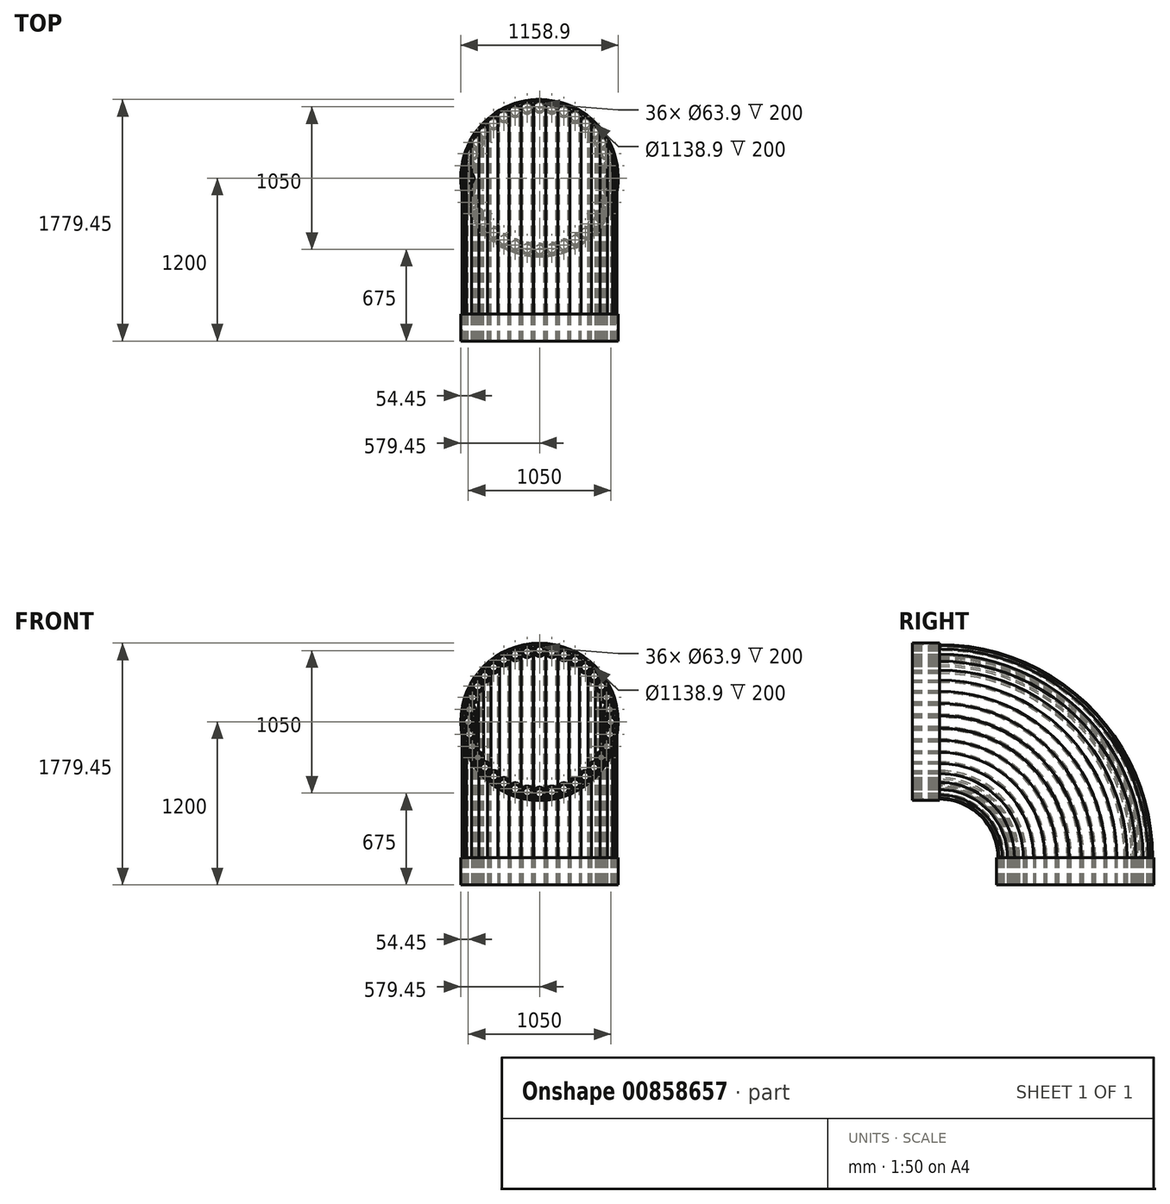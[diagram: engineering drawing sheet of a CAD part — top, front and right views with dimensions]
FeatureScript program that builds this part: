
annotation { "Feature Type Name" : "Feature", "Feature Type Description" : "" }
export const myFeature = defineFeature(function(context is Context, id is Id, definition is map)
    precondition{}
    {
        {
            var Q0;
            Q0=qCreatedBy(makeId("Front.planeOp"),FACE);
            var sketch = newSketch(context, id + "F0", { "sketchPlane" : qUnion([Q0])});
            skCircle(sketch, "E0", {"center": v(0, 0) * mm, "radius": 525 * mm, "construction": true});
            skCircle(sketch, "E1", {"center": v(0, 525) * mm, "radius": 44.45 * mm});
            skCircle(sketch, "E2", {"center": v(0, 525) * mm, "radius": 31.95 * mm});
            skCircle(sketch, "E3.1.0", {"center": v(-91.17, 517.02) * mm, "radius": 44.45 * mm});
            skCircle(sketch, "E3.1.1", {"center": v(-91.17, 517.02) * mm, "radius": 31.95 * mm});
            skCircle(sketch, "E3.2.0", {"center": v(-179.56, 493.34) * mm, "radius": 44.45 * mm});
            skCircle(sketch, "E3.2.1", {"center": v(-179.56, 493.34) * mm, "radius": 31.95 * mm});
            skCircle(sketch, "E3.3.0", {"center": v(-262.5, 454.66) * mm, "radius": 44.45 * mm});
            skCircle(sketch, "E3.3.1", {"center": v(-262.5, 454.66) * mm, "radius": 31.95 * mm});
            skCircle(sketch, "E3.4.0", {"center": v(-337.46, 402.17) * mm, "radius": 44.45 * mm});
            skCircle(sketch, "E3.4.1", {"center": v(-337.46, 402.17) * mm, "radius": 31.95 * mm});
            skCircle(sketch, "E3.5.0", {"center": v(-402.17, 337.46) * mm, "radius": 44.45 * mm});
            skCircle(sketch, "E3.5.1", {"center": v(-402.17, 337.46) * mm, "radius": 31.95 * mm});
            skCircle(sketch, "E3.6.0", {"center": v(-454.66, 262.5) * mm, "radius": 44.45 * mm});
            skCircle(sketch, "E3.6.1", {"center": v(-454.66, 262.5) * mm, "radius": 31.95 * mm});
            skCircle(sketch, "E3.7.0", {"center": v(-493.34, 179.56) * mm, "radius": 44.45 * mm});
            skCircle(sketch, "E3.7.1", {"center": v(-493.34, 179.56) * mm, "radius": 31.95 * mm});
            skCircle(sketch, "E3.8.0", {"center": v(-517.02, 91.17) * mm, "radius": 44.45 * mm});
            skCircle(sketch, "E3.8.1", {"center": v(-517.02, 91.17) * mm, "radius": 31.95 * mm});
            skCircle(sketch, "E3.9.0", {"center": v(-525, 0) * mm, "radius": 44.45 * mm});
            skCircle(sketch, "E3.9.1", {"center": v(-525, 0) * mm, "radius": 31.95 * mm});
            skCircle(sketch, "E3.10.0", {"center": v(-517.02, -91.17) * mm, "radius": 44.45 * mm});
            skCircle(sketch, "E3.10.1", {"center": v(-517.02, -91.17) * mm, "radius": 31.95 * mm});
            skCircle(sketch, "E3.11.0", {"center": v(-493.34, -179.56) * mm, "radius": 44.45 * mm});
            skCircle(sketch, "E3.11.1", {"center": v(-493.34, -179.56) * mm, "radius": 31.95 * mm});
            skCircle(sketch, "E3.12.0", {"center": v(-454.66, -262.5) * mm, "radius": 44.45 * mm});
            skCircle(sketch, "E3.12.1", {"center": v(-454.66, -262.5) * mm, "radius": 31.95 * mm});
            skCircle(sketch, "E3.13.0", {"center": v(-402.17, -337.46) * mm, "radius": 44.45 * mm});
            skCircle(sketch, "E3.13.1", {"center": v(-402.17, -337.46) * mm, "radius": 31.95 * mm});
            skCircle(sketch, "E3.14.0", {"center": v(-337.46, -402.17) * mm, "radius": 44.45 * mm});
            skCircle(sketch, "E3.14.1", {"center": v(-337.46, -402.17) * mm, "radius": 31.95 * mm});
            skCircle(sketch, "E3.15.0", {"center": v(-262.5, -454.66) * mm, "radius": 44.45 * mm});
            skCircle(sketch, "E3.15.1", {"center": v(-262.5, -454.66) * mm, "radius": 31.95 * mm});
            skCircle(sketch, "E3.16.0", {"center": v(-179.56, -493.34) * mm, "radius": 44.45 * mm});
            skCircle(sketch, "E3.16.1", {"center": v(-179.56, -493.34) * mm, "radius": 31.95 * mm});
            skCircle(sketch, "E3.17.0", {"center": v(-91.17, -517.02) * mm, "radius": 44.45 * mm});
            skCircle(sketch, "E3.17.1", {"center": v(-91.17, -517.02) * mm, "radius": 31.95 * mm});
            skCircle(sketch, "E3.18.0", {"center": v(0, -525) * mm, "radius": 44.45 * mm});
            skCircle(sketch, "E3.18.1", {"center": v(0, -525) * mm, "radius": 31.95 * mm});
            skCircle(sketch, "E3.19.0", {"center": v(91.17, -517.02) * mm, "radius": 44.45 * mm});
            skCircle(sketch, "E3.19.1", {"center": v(91.17, -517.02) * mm, "radius": 31.95 * mm});
            skCircle(sketch, "E3.20.0", {"center": v(179.56, -493.34) * mm, "radius": 44.45 * mm});
            skCircle(sketch, "E3.20.1", {"center": v(179.56, -493.34) * mm, "radius": 31.95 * mm});
            skCircle(sketch, "E3.21.0", {"center": v(262.5, -454.66) * mm, "radius": 44.45 * mm});
            skCircle(sketch, "E3.21.1", {"center": v(262.5, -454.66) * mm, "radius": 31.95 * mm});
            skCircle(sketch, "E3.22.0", {"center": v(337.46, -402.17) * mm, "radius": 44.45 * mm});
            skCircle(sketch, "E3.22.1", {"center": v(337.46, -402.17) * mm, "radius": 31.95 * mm});
            skCircle(sketch, "E3.23.0", {"center": v(402.17, -337.46) * mm, "radius": 44.45 * mm});
            skCircle(sketch, "E3.23.1", {"center": v(402.17, -337.46) * mm, "radius": 31.95 * mm});
            skCircle(sketch, "E3.24.0", {"center": v(454.66, -262.5) * mm, "radius": 44.45 * mm});
            skCircle(sketch, "E3.24.1", {"center": v(454.66, -262.5) * mm, "radius": 31.95 * mm});
            skCircle(sketch, "E3.25.0", {"center": v(493.34, -179.56) * mm, "radius": 44.45 * mm});
            skCircle(sketch, "E3.25.1", {"center": v(493.34, -179.56) * mm, "radius": 31.95 * mm});
            skCircle(sketch, "E3.26.0", {"center": v(517.02, -91.17) * mm, "radius": 44.45 * mm});
            skCircle(sketch, "E3.26.1", {"center": v(517.02, -91.17) * mm, "radius": 31.95 * mm});
            skCircle(sketch, "E3.27.0", {"center": v(525, 0) * mm, "radius": 44.45 * mm});
            skCircle(sketch, "E3.27.1", {"center": v(525, 0) * mm, "radius": 31.95 * mm});
            skCircle(sketch, "E3.28.0", {"center": v(517.02, 91.17) * mm, "radius": 44.45 * mm});
            skCircle(sketch, "E3.28.1", {"center": v(517.02, 91.17) * mm, "radius": 31.95 * mm});
            skCircle(sketch, "E3.29.0", {"center": v(493.34, 179.56) * mm, "radius": 44.45 * mm});
            skCircle(sketch, "E3.29.1", {"center": v(493.34, 179.56) * mm, "radius": 31.95 * mm});
            skCircle(sketch, "E3.30.0", {"center": v(454.66, 262.5) * mm, "radius": 44.45 * mm});
            skCircle(sketch, "E3.30.1", {"center": v(454.66, 262.5) * mm, "radius": 31.95 * mm});
            skCircle(sketch, "E3.31.0", {"center": v(402.17, 337.46) * mm, "radius": 44.45 * mm});
            skCircle(sketch, "E3.31.1", {"center": v(402.17, 337.46) * mm, "radius": 31.95 * mm});
            skCircle(sketch, "E3.32.0", {"center": v(337.46, 402.17) * mm, "radius": 44.45 * mm});
            skCircle(sketch, "E3.32.1", {"center": v(337.46, 402.17) * mm, "radius": 31.95 * mm});
            skCircle(sketch, "E3.33.0", {"center": v(262.5, 454.66) * mm, "radius": 44.45 * mm});
            skCircle(sketch, "E3.33.1", {"center": v(262.5, 454.66) * mm, "radius": 31.95 * mm});
            skCircle(sketch, "E3.34.0", {"center": v(179.56, 493.34) * mm, "radius": 44.45 * mm});
            skCircle(sketch, "E3.34.1", {"center": v(179.56, 493.34) * mm, "radius": 31.95 * mm});
            skCircle(sketch, "E3.35.0", {"center": v(91.17, 517.02) * mm, "radius": 44.45 * mm});
            skCircle(sketch, "E3.35.1", {"center": v(91.17, 517.02) * mm, "radius": 31.95 * mm});
            skSolve(sketch);
        }
        {
            var Q0;
            Q0=qCreatedBy(makeId("Right.planeOp"),FACE);
            var sketch = newSketch(context, id + "F1", { "sketchPlane" : qUnion([Q0])});
            skLineSegment(sketch, "E4", {"start": v(0, 0) * mm, "end": v(200, 0) * mm});
            skLineSegment(sketch, "E5", {"start": v(1200, -1000) * mm, "end": v(1200, -1200) * mm});
            skPoint(sketch, "E6.visualSharp", {"position": v(1200, 0) * mm});
            skArc(sketch, "E6.filletArc", {"start": v(1200, -1000) * mm, "mid": v(907.1, -292.9) * mm, "end": v(200, 0) * mm});
            skSolve(sketch);
        }
        {
            var Q0;
            Q0 = qSketchRegion(id + "F0", true);
            var Q1;
            Q1 = qConstructionFilter(qBodyType(qCreatedBy(id + "F1" ,EDGE), BodyType.WIRE), ConstructionObject.NO);
            sweep(context, id + "F2", {"profiles" : qUnion([Q0]), "path" : qUnion([Q1])});
        }
        {
            var Q0;
            Q0=qCreatedBy(makeId("Front.planeOp"),FACE);
            var sketch = newSketch(context, id + "F3", { "sketchPlane" : qUnion([Q0])});
            skCircle(sketch, "E7", {"center": v(0, 0) * mm, "radius": 569.45 * mm});
            skCircle(sketch, "E8.0", {"center": v(0, 0) * mm, "radius": 579.45 * mm});
            skSolve(sketch);
        }
        {
            var Q0;
            Q0 = qSketchRegion(id + "F3", true);
            extrude(context, id + "F4", {"entities" : qUnion([Q0]), "oppositeDirection" : true, "depth" : 200 * mm, "offsetDistance" : 25 * mm});
        }
        {
            var Q0;
            Q0=sQuery(id+"F1.wireOp",VERTEX,"E5.end");
            var Q1;
            Q1=sQuery(id+"F1.wireOp",EDGE,"E5");
            cPlane(context, id + "F5", {"entities" : qUnion([Q0, Q1]), "cplaneType" : CPlaneType.LINE_POINT, "offset" : 25 * mm, "width" : 150 * mm, "height" : 150 * mm});
        }
        {
            var Q0;
            Q0=qCreatedBy(id+"F5.planeOp",FACE);
            var sketch = newSketch(context, id + "F6", { "sketchPlane" : qUnion([Q0])});
            skCircle(sketch, "E9", {"center": v(0, -1200) * mm, "radius": 569.45 * mm});
            skCircle(sketch, "E10.0", {"center": v(0, -1200) * mm, "radius": 579.45 * mm});
            skSolve(sketch);
        }
        {
            var Q0;
            Q0 = qSketchRegion(id + "F6", true);
            extrude(context, id + "F7", {"entities" : qUnion([Q0]), "oppositeDirection" : true, "depth" : 200 * mm, "offsetDistance" : 25 * mm});
        }
    });
